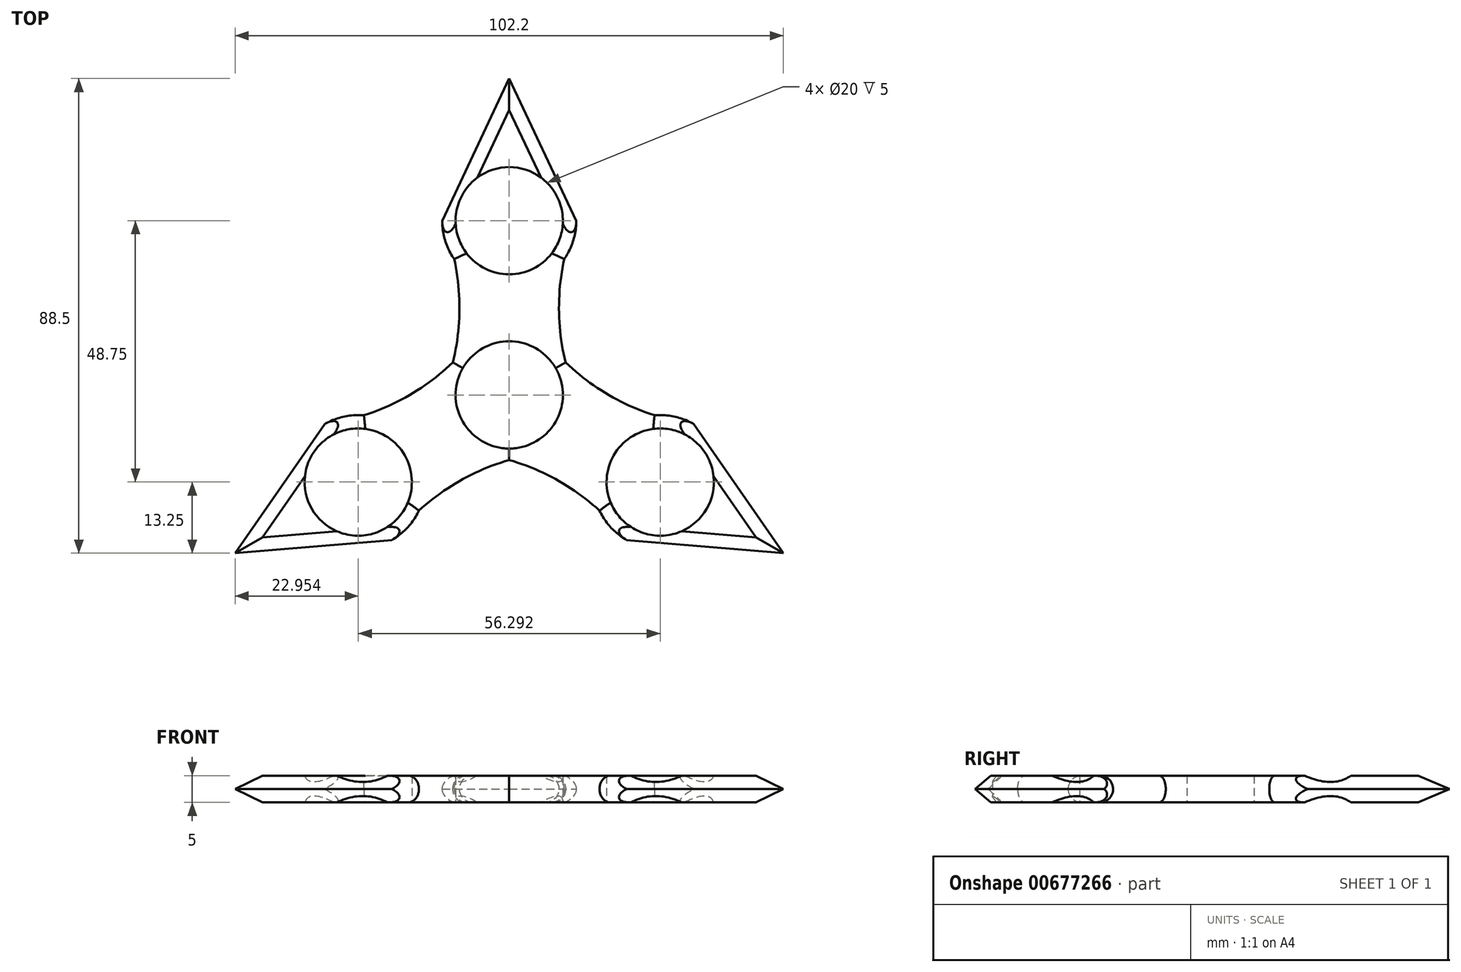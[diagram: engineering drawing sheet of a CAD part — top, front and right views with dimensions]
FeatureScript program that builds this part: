
annotation { "Feature Type Name" : "Feature", "Feature Type Description" : "" }
export const myFeature = defineFeature(function(context is Context, id is Id, definition is map)
    precondition{}
    {
        {
            var Q0;
            Q0=qCreatedBy(makeId("Top.planeOp"),FACE);
            var sketch = newSketch(context, id + "F0", { "sketchPlane" : qUnion([Q0])});
            skArc(sketch, "E0", {"start": v(-6.85, 44.48) * mm, "mid": v(-38.97, 22.5) * mm, "end": v(-41.94, -16.3) * mm});
            skCircle(sketch, "E1", {"center": v(0, 0) * mm, "radius": 10 * mm});
            skCircle(sketch, "E2", {"center": v(0, 32.5) * mm, "radius": 10 * mm});
            skArc(sketch, "E3", {"start": v(10.26, 25.36) * mm, "mid": v(11.93, 28.76) * mm, "end": v(12.5, 32.5) * mm});
            skLineSegment(sketch, "E4", {"start": v(0, 32.5) * mm, "end": v(-10, 32.5) * mm});
            skArc(sketch, "E5", {"start": v(-10.5, 6.07) * mm, "mid": v(-9.27, 15.7) * mm, "end": v(-10.26, 25.36) * mm});
            skLineSegment(sketch, "E6", {"start": v(0, 32.5) * mm, "end": v(10, 32.5) * mm});
            skArc(sketch, "E7", {"start": v(10.26, 25.36) * mm, "mid": v(9.27, 15.7) * mm, "end": v(10.5, 6.07) * mm});
            skArc(sketch, "E8.1.0", {"start": v(-27.09, -3.8) * mm, "mid": v(-30.87, -4.05) * mm, "end": v(-34.4, -5.42) * mm});
            skCircle(sketch, "E8.1.1", {"center": v(-28.15, -16.25) * mm, "radius": 10 * mm});
            skArc(sketch, "E8.1.2", {"start": v(0, -12.13) * mm, "mid": v(-8.96, -15.88) * mm, "end": v(-16.83, -21.56) * mm});
            skArc(sketch, "E8.1.3", {"start": v(-27.09, -3.8) * mm, "mid": v(-18.23, 0.18) * mm, "end": v(-10.5, 6.07) * mm});
            skArc(sketch, "E8.2.0", {"start": v(16.83, -21.56) * mm, "mid": v(18.94, -24.7) * mm, "end": v(21.9, -27.08) * mm});
            skCircle(sketch, "E8.2.1", {"center": v(28.15, -16.25) * mm, "radius": 10 * mm});
            skArc(sketch, "E8.2.2", {"start": v(10.5, 6.07) * mm, "mid": v(18.23, 0.18) * mm, "end": v(27.09, -3.8) * mm});
            skArc(sketch, "E8.2.3", {"start": v(16.83, -21.56) * mm, "mid": v(8.96, -15.88) * mm, "end": v(0, -12.13) * mm});
            skPoint(sketch, "E9.orphan", {"position": v(-12.5, 0) * mm});
            skPoint(sketch, "E10.orphan", {"position": v(-6.25, 10.83) * mm});
            skPoint(sketch, "E11.orphan", {"position": v(6.25, 10.83) * mm});
            skPoint(sketch, "E12.orphan", {"position": v(12.5, 0) * mm});
            skPoint(sketch, "E13.orphan", {"position": v(6.25, -10.83) * mm});
            skPoint(sketch, "E14.orphan", {"position": v(-6.25, -10.83) * mm});
            skLineSegment(sketch, "E15", {"start": v(12.5, 32.5) * mm, "end": v(0, 59) * mm});
            skPoint(sketch, "E15.endSnap0", {"position": v(0, 45) * mm});
            skLineSegment(sketch, "E16", {"start": v(0, 59) * mm, "end": v(-12.5, 32.5) * mm});
            skLineSegment(sketch, "E17.1.0", {"start": v(-34.4, -5.42) * mm, "end": v(-51.1, -29.5) * mm});
            skLineSegment(sketch, "E17.1.1", {"start": v(-51.1, -29.5) * mm, "end": v(-21.9, -27.08) * mm});
            skLineSegment(sketch, "E17.2.0", {"start": v(21.9, -27.08) * mm, "end": v(51.1, -29.5) * mm});
            skLineSegment(sketch, "E17.2.1", {"start": v(51.1, -29.5) * mm, "end": v(34.4, -5.42) * mm});
            skArc(sketch, "E18.trimOffspring", {"start": v(-21.9, -27.08) * mm, "mid": v(-18.94, -24.7) * mm, "end": v(-16.83, -21.56) * mm});
            skArc(sketch, "E19.trimOffspring", {"start": v(34.4, -5.42) * mm, "mid": v(30.87, -4.05) * mm, "end": v(27.09, -3.8) * mm});
            skArc(sketch, "E20.trimOffspring", {"start": v(-12.5, 32.5) * mm, "mid": v(-11.93, 28.76) * mm, "end": v(-10.26, 25.36) * mm});
            skArc(sketch, "E21.trimOffspring", {"start": v(41.94, -16.3) * mm, "mid": v(38.97, 22.5) * mm, "end": v(6.85, 44.48) * mm});
            skArc(sketch, "E22.trimOffspring", {"start": v(-35.1, -28.17) * mm, "mid": v(0, -45) * mm, "end": v(35.1, -28.17) * mm});
            skSolve(sketch);
        }
        {
            var Q0;
            Q0=makeQuery(id+"F0.imprint","IMPRINT",FACE,{"disambiguationData":[TD([[makeQuery(id+"F0.imprint","IMPRINT",EDGE,{"derivedFrom":sQuery(id+"F0.wireOp",EDGE,"E1")}),-1.0]])]});
            extrude(context, id + "F1", {"entities" : qUnion([Q0]), "depth" : 5 * mm, "offsetDistance" : 25 * mm});
        }
        {
            var Q0;
            Q0=makeQuery(id+"F1.opExtrude","CAP_EDGE",EDGE,{"disambiguationData":[OSD([sQuery(id+"F0.wireOp",EDGE,"E17.1.1")])],"isStart":false});
            var Q1;
            Q1=makeQuery(id+"F1.opExtrude","CAP_EDGE",EDGE,{"disambiguationData":[OSD([sQuery(id+"F0.wireOp",EDGE,"E17.1.0")])],"isStart":false});
            var Q2;
            Q2=makeQuery(id+"F1.opExtrude","CAP_EDGE",EDGE,{"disambiguationData":[OSD([sQuery(id+"F0.wireOp",EDGE,"E17.1.1")])],"isStart":true});
            var Q3;
            Q3=makeQuery(id+"F1.opExtrude","CAP_EDGE",EDGE,{"disambiguationData":[OSD([sQuery(id+"F0.wireOp",EDGE,"E17.1.0")])],"isStart":true});
            var Q4;
            Q4=makeQuery(id+"F1.opExtrude","CAP_EDGE",EDGE,{"disambiguationData":[OSD([sQuery(id+"F0.wireOp",EDGE,"E17.2.0")])],"isStart":true});
            var Q5;
            Q5=makeQuery(id+"F1.opExtrude","CAP_EDGE",EDGE,{"disambiguationData":[OSD([sQuery(id+"F0.wireOp",EDGE,"E17.2.0")])],"isStart":false});
            var Q6;
            Q6=makeQuery(id+"F1.opExtrude","CAP_EDGE",EDGE,{"disambiguationData":[OSD([sQuery(id+"F0.wireOp",EDGE,"E17.2.1")])],"isStart":false});
            var Q7;
            Q7=makeQuery(id+"F1.opExtrude","CAP_EDGE",EDGE,{"disambiguationData":[OSD([sQuery(id+"F0.wireOp",EDGE,"E17.2.1")])],"isStart":true});
            var Q8;
            Q8=makeQuery(id+"F1.opExtrude","CAP_EDGE",EDGE,{"disambiguationData":[OSD([sQuery(id+"F0.wireOp",EDGE,"E15")])],"isStart":false});
            var Q9;
            Q9=makeQuery(id+"F1.opExtrude","CAP_EDGE",EDGE,{"disambiguationData":[OSD([sQuery(id+"F0.wireOp",EDGE,"E15")])],"isStart":true});
            var Q10;
            Q10=makeQuery(id+"F1.opExtrude","CAP_EDGE",EDGE,{"disambiguationData":[OSD([sQuery(id+"F0.wireOp",EDGE,"E16")])],"isStart":true});
            var Q11;
            Q11=makeQuery(id+"F1.opExtrude","CAP_EDGE",EDGE,{"disambiguationData":[OSD([sQuery(id+"F0.wireOp",EDGE,"E16")])],"isStart":false});
            chamfer(context, id + "F2", {"entities" : qUnion([Q0, Q1, Q2, Q3, Q4, Q5, Q6, Q7, Q8, Q9, Q10, Q11]), "width" : 2.5 * mm, "tangentPropagation" : true});
        }
        {
            var Q0;
            Q0=makeQuery(id+"F1.opExtrude","CAP_EDGE",EDGE,{"disambiguationData":[OSD([sQuery(id+"F0.wireOp",EDGE,"E8.1.2")])],"isStart":false});
            var Q1;
            Q1=makeQuery(id+"F1.opExtrude","CAP_EDGE",EDGE,{"disambiguationData":[OSD([sQuery(id+"F0.wireOp",EDGE,"E8.1.2")])],"isStart":true});
            var Q2;
            Q2=makeQuery(id+"F1.opExtrude","CAP_EDGE",EDGE,{"disambiguationData":[OSD([sQuery(id+"F0.wireOp",EDGE,"E18.trimOffspring")])],"isStart":false});
            var Q3;
            Q3=makeQuery(id+"F1.opExtrude","CAP_EDGE",EDGE,{"disambiguationData":[OSD([sQuery(id+"F0.wireOp",EDGE,"E18.trimOffspring")])],"isStart":true});
            var Q4;
            Q4=makeQuery(id+"F1.opExtrude","CAP_EDGE",EDGE,{"disambiguationData":[OSD([sQuery(id+"F0.wireOp",EDGE,"E8.2.3")])],"isStart":false});
            var Q5;
            Q5=makeQuery(id+"F1.opExtrude","CAP_EDGE",EDGE,{"disambiguationData":[OSD([sQuery(id+"F0.wireOp",EDGE,"E8.2.3")])],"isStart":true});
            var Q6;
            Q6=makeQuery(id+"F1.opExtrude","CAP_EDGE",EDGE,{"disambiguationData":[OSD([sQuery(id+"F0.wireOp",EDGE,"E8.2.0")])],"isStart":false});
            var Q7;
            Q7=makeQuery(id+"F1.opExtrude","CAP_EDGE",EDGE,{"disambiguationData":[OSD([sQuery(id+"F0.wireOp",EDGE,"E8.2.0")])],"isStart":true});
            var Q8;
            Q8=makeQuery(id+"F1.opExtrude","CAP_EDGE",EDGE,{"disambiguationData":[OSD([sQuery(id+"F0.wireOp",EDGE,"E8.2.2")])],"isStart":false});
            var Q9;
            Q9=makeQuery(id+"F1.opExtrude","CAP_EDGE",EDGE,{"disambiguationData":[OSD([sQuery(id+"F0.wireOp",EDGE,"E19.trimOffspring")])],"isStart":false});
            var Q10;
            Q10=makeQuery(id+"F1.opExtrude","CAP_EDGE",EDGE,{"disambiguationData":[OSD([sQuery(id+"F0.wireOp",EDGE,"E7")])],"isStart":false});
            var Q11;
            Q11=makeQuery(id+"F1.opExtrude","CAP_EDGE",EDGE,{"disambiguationData":[OSD([sQuery(id+"F0.wireOp",EDGE,"E3")])],"isStart":false});
            var Q12;
            Q12=makeQuery(id+"F1.opExtrude","CAP_EDGE",EDGE,{"disambiguationData":[OSD([sQuery(id+"F0.wireOp",EDGE,"E19.trimOffspring")])],"isStart":true});
            var Q13;
            Q13=makeQuery(id+"F1.opExtrude","CAP_EDGE",EDGE,{"disambiguationData":[OSD([sQuery(id+"F0.wireOp",EDGE,"E8.2.2")])],"isStart":true});
            var Q14;
            Q14=makeQuery(id+"F1.opExtrude","CAP_EDGE",EDGE,{"disambiguationData":[OSD([sQuery(id+"F0.wireOp",EDGE,"E7")])],"isStart":true});
            var Q15;
            Q15=makeQuery(id+"F1.opExtrude","CAP_EDGE",EDGE,{"disambiguationData":[OSD([sQuery(id+"F0.wireOp",EDGE,"E3")])],"isStart":true});
            var Q16;
            Q16=makeQuery(id+"F1.opExtrude","CAP_EDGE",EDGE,{"disambiguationData":[OSD([sQuery(id+"F0.wireOp",EDGE,"E8.1.3")])],"isStart":true});
            var Q17;
            Q17=makeQuery(id+"F1.opExtrude","CAP_EDGE",EDGE,{"disambiguationData":[OSD([sQuery(id+"F0.wireOp",EDGE,"E8.1.0")])],"isStart":true});
            var Q18;
            Q18=makeQuery(id+"F1.opExtrude","CAP_EDGE",EDGE,{"disambiguationData":[OSD([sQuery(id+"F0.wireOp",EDGE,"E5")])],"isStart":true});
            var Q19;
            Q19=makeQuery(id+"F1.opExtrude","CAP_EDGE",EDGE,{"disambiguationData":[OSD([sQuery(id+"F0.wireOp",EDGE,"E20.trimOffspring")])],"isStart":true});
            var Q20;
            Q20=makeQuery(id+"F1.opExtrude","CAP_EDGE",EDGE,{"disambiguationData":[OSD([sQuery(id+"F0.wireOp",EDGE,"E8.1.3")])],"isStart":false});
            var Q21;
            Q21=makeQuery(id+"F1.opExtrude","CAP_EDGE",EDGE,{"disambiguationData":[OSD([sQuery(id+"F0.wireOp",EDGE,"E8.1.0")])],"isStart":false});
            var Q22;
            Q22=makeQuery(id+"F1.opExtrude","CAP_EDGE",EDGE,{"disambiguationData":[OSD([sQuery(id+"F0.wireOp",EDGE,"E5")])],"isStart":false});
            var Q23;
            Q23=makeQuery(id+"F1.opExtrude","CAP_EDGE",EDGE,{"disambiguationData":[OSD([sQuery(id+"F0.wireOp",EDGE,"E20.trimOffspring")])],"isStart":false});
            fillet(context, id + "F3", {"entities" : qUnion([Q0, Q1, Q2, Q3, Q4, Q5, Q6, Q7, Q8, Q9, Q10, Q11, Q12, Q13, Q14, Q15, Q16, Q17, Q18, Q19, Q20, Q21, Q22, Q23]), "radius" : 2.5 * mm, "tangentPropagation" : true, "allowEdgeOverflow" : false});
        }
    });
